# Revit family: mcr FID-120-НЗ-К3-ВН-АхВ ЗМ
name_source: partatom
category: Арматура воздуховодов
revit_build: Autodesk Revit 2016 (Build: 20150714_1515(x64)
units: mm (PartAtom-declared; Revit-internal decimal feet)

## family parameters
Всегда вертикально = Да
На основе рабочей плоскости = Нет
Общий = Да
При загрузке вырезать с полостями = Нет
Размер круглого соединителя = Использовать радиус
Тип детали = Вставляется

## types (1)
- mcr FID-120-НЗ-К3-ВН-АхВ ЗМ
    ADSK_Масса = 0
    BE230 = Нет
    BE24 = Нет
    BF230 = Нет
    BF24 = Нет
    BFL230 = Нет
    BFL24 = Нет
    BFN230 = Нет
    BFN24 = Нет
    BLE230 = Нет
    BLE24 = Нет
    MM230 = Нет
    MM24 = Нет
    P = 1.2000 кг/куб. м
    Глубина клапана = 220 мм
    До оси привода = 100 мм
    Материал клапана = <По категории>
    Оснащение привода саморегулирующимся нагревательным кабелем = Нет
    Термодатчик = Нет
    Толщина заслонки = 20 мм
    Толщина стенки = 10 мм

## geometry (parser evidence)
native form markers: Blend x4
no freeform markers — native parametric forms only
